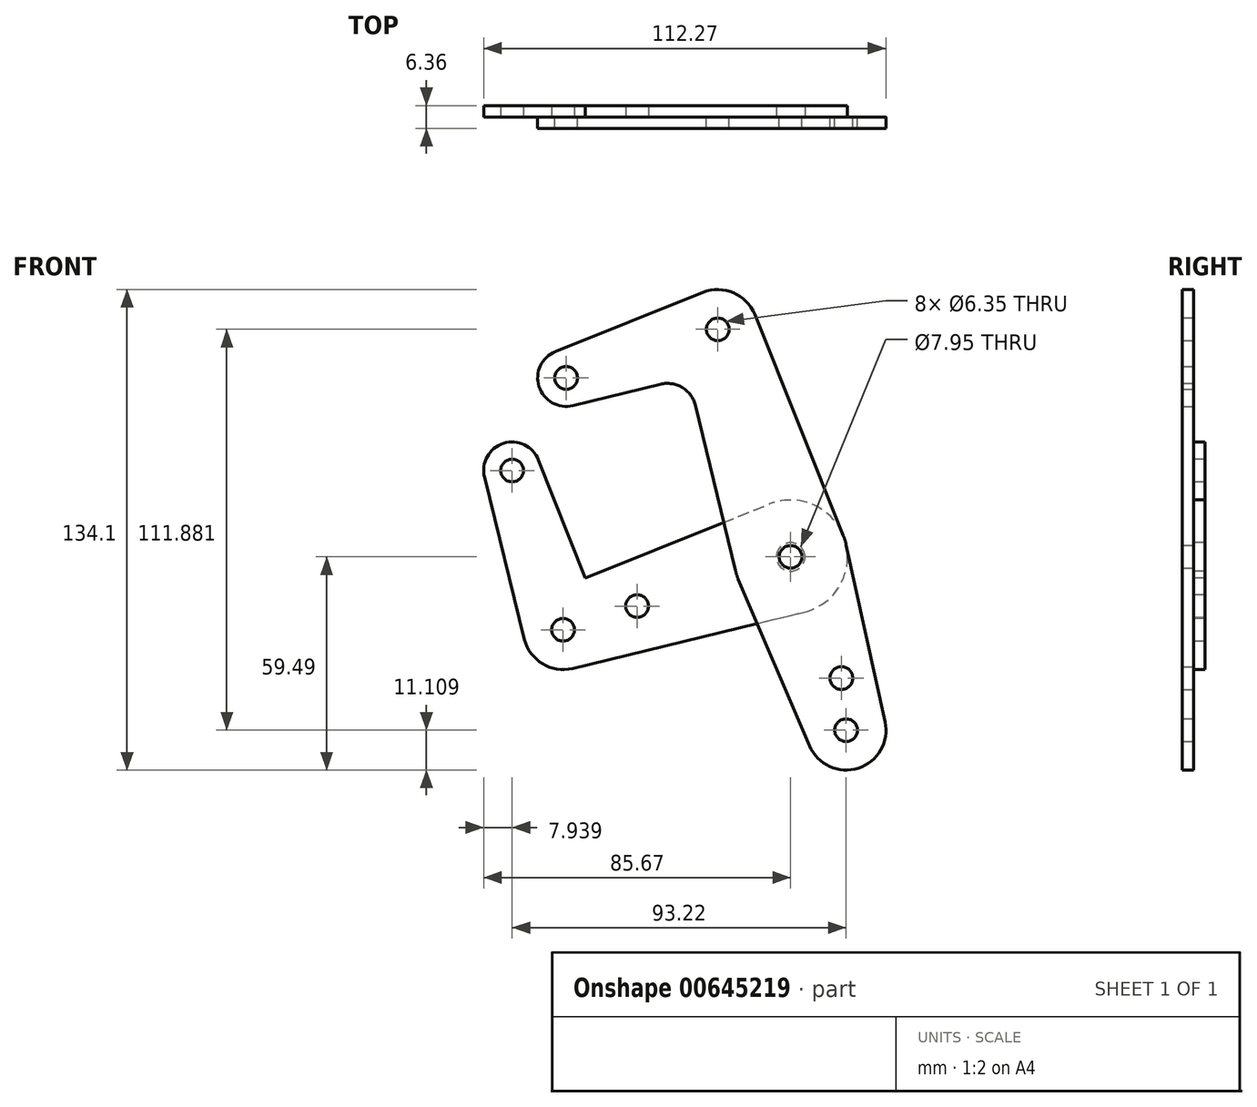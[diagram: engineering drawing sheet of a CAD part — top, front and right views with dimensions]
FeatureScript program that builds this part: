
annotation { "Feature Type Name" : "Feature", "Feature Type Description" : "" }
export const myFeature = defineFeature(function(context is Context, id is Id, definition is map)
    precondition{}
    {
        {
            var Q0;
            Q0=qCreatedBy(makeId("Front.planeOp"),FACE);
            var sketch = newSketch(context, id + "F0", { "sketchPlane" : qUnion([Q0])});
            skCircle(sketch, "E0", {"center": v(-62.66, 49.95) * mm, "radius": 7.94 * mm});
            skCircle(sketch, "E1", {"center": v(-20.33, 63.5) * mm, "radius": 11.11 * mm});
            skCircle(sketch, "E2", {"center": v(0, 0) * mm, "radius": 15.88 * mm});
            skCircle(sketch, "E3", {"center": v(15.49, -48.38) * mm, "radius": 11.11 * mm});
            skCircle(sketch, "E4", {"center": v(14.16, -33.82) * mm, "radius": 3.17 * mm});
            skLineSegment(sketch, "E5", {"start": v(-27.48, 85.85) * mm, "end": v(19.13, -59.77) * mm, "construction": true});
            skLineSegment(sketch, "E6", {"start": v(0, 0) * mm, "end": v(60.36, 19.32) * mm, "construction": true});
            skLineSegment(sketch, "E7", {"start": v(-77.14, 45.31) * mm, "end": v(-2.1, 69.33) * mm, "construction": true});
            skCircle(sketch, "E8", {"center": v(15.49, -48.38) * mm, "radius": 3.18 * mm});
            skCircle(sketch, "E9", {"center": v(0, 0) * mm, "radius": 3.98 * mm});
            skCircle(sketch, "E10", {"center": v(0, 0) * mm, "radius": 3.18 * mm});
            skCircle(sketch, "E11", {"center": v(-20.33, 63.5) * mm, "radius": 3.18 * mm});
            skCircle(sketch, "E12", {"center": v(-62.66, 49.95) * mm, "radius": 3.18 * mm});
            skLineSegment(sketch, "E13", {"start": v(14.16, -33.82) * mm, "end": v(22.72, -60.54) * mm, "construction": true});
            skLineSegment(sketch, "E14", {"start": v(-65.62, 57.31) * mm, "end": v(-24.47, 73.81) * mm});
            skLineSegment(sketch, "E15", {"start": v(-10.02, 67.64) * mm, "end": v(14.73, 5.9) * mm});
            skLineSegment(sketch, "E16", {"start": v(5.27, -52.75) * mm, "end": v(-14.6, -6.24) * mm});
            skLineSegment(sketch, "E17", {"start": v(-15.43, -3.75) * mm, "end": v(-26.63, 42.35) * mm});
            skLineSegment(sketch, "E18", {"start": v(26.34, -46) * mm, "end": v(15.5, 3.4) * mm});
            skLineSegment(sketch, "E19", {"start": v(-60.79, 42.23) * mm, "end": v(-36.23, 48.2) * mm});
            skArc(sketch, "E20.filletArc", {"start": v(-26.63, 42.35) * mm, "mid": v(-30.22, 47.27) * mm, "end": v(-36.23, 48.2) * mm});
            skLineSegment(sketch, "E21", {"start": v(0, 0) * mm, "end": v(-85.7, -27.44) * mm, "construction": true});
            skLineSegment(sketch, "E22", {"start": v(-76.14, 19.16) * mm, "end": v(-54.17, -49.48) * mm, "construction": true});
            skCircle(sketch, "E23", {"center": v(-42.85, -13.72) * mm, "radius": 3.18 * mm});
            skCircle(sketch, "E24", {"center": v(-63.5, -20.33) * mm, "radius": 11.11 * mm});
            skCircle(sketch, "E25", {"center": v(-77.73, 24.12) * mm, "radius": 7.94 * mm});
            skCircle(sketch, "E26", {"center": v(-63.5, -20.33) * mm, "radius": 3.18 * mm});
            skCircle(sketch, "E27", {"center": v(-77.73, 24.12) * mm, "radius": 3.18 * mm});
            skLineSegment(sketch, "E28", {"start": v(-70.35, 27.05) * mm, "end": v(-53.17, -16.23) * mm});
            skLineSegment(sketch, "E29", {"start": v(-85.44, 22.22) * mm, "end": v(-74.29, -23) * mm});
            skLineSegment(sketch, "E30", {"start": v(-60.88, -31.13) * mm, "end": v(3.75, -15.43) * mm});
            skLineSegment(sketch, "E31", {"start": v(-67.64, -10.02) * mm, "end": v(-5.9, 14.73) * mm});
            skSolve(sketch);
        }
        {
            var Q0;
            {var subQ4=sQuery(id+"F0.wireOp",EDGE,"E14");Q0=makeQuery(id+"F0.imprint","IMPRINT",FACE,{"disambiguationData":[TD([[makeQuery(id+"F0.imprint","IMPRINT",EDGE,{"derivedFrom":subQ4}),-1.0]])]});}
            var Q1;
            Q1=makeQuery(id+"F0.imprint","IMPRINT",FACE,{"disambiguationData":[TD([[makeQuery(id+"F0.imprint","IMPRINT",EDGE,{"derivedFrom":sQuery(id+"F0.wireOp",EDGE,"E4")}),-1.0]])]});
            var Q2;
            Q2=makeQuery(id+"F0.imprint","IMPRINT",FACE,{"disambiguationData":[TD([[makeQuery(id+"F0.imprint","IMPRINT",EDGE,{"derivedFrom":sQuery(id+"F0.wireOp",EDGE,"E9")}),-1.0]])]});
            var Q3;
            Q3=makeQuery(id+"F0.imprint","IMPRINT",FACE,{"disambiguationData":[TD([[makeQuery(id+"F0.imprint","IMPRINT",EDGE,{"derivedFrom":sQuery(id+"F0.wireOp",EDGE,"E9")}),1.0]])]});
            var Q4;
            Q4=makeQuery(id+"F0.imprint","IMPRINT",FACE,{"disambiguationData":[TD([[makeQuery(id+"F0.imprint","IMPRINT",EDGE,{"derivedFrom":sQuery(id+"F0.wireOp",EDGE,"E8")}),-1.0]])]});
            var Q5;
            Q5=makeQuery(id+"F0.imprint","IMPRINT",FACE,{"disambiguationData":[TD([[makeQuery(id+"F0.imprint","IMPRINT",EDGE,{"derivedFrom":sQuery(id+"F0.wireOp",EDGE,"E11")}),-1.0]])]});
            var Q6;
            Q6=makeQuery(id+"F0.imprint","IMPRINT",FACE,{"disambiguationData":[TD([[makeQuery(id+"F0.imprint","IMPRINT",EDGE,{"derivedFrom":sQuery(id+"F0.wireOp",EDGE,"E12")}),-1.0]])]});
            var Q7;
            {var subQ0=sQuery(id+"F0.wireOp",EDGE,"E17");var subQ1=sQuery(id+"F0.wireOp",EDGE,"E2");var subQ2=makeQuery(id+"F0.imprint","INTERSECT",VERTEX,{"derivedFrom":[subQ1,subQ0]});Q7=makeQuery(id+"F0.imprint","IMPRINT",FACE,{"disambiguationData":[TD([[makeQuery(id+"F0.imprint","IMPRINT",EDGE,{"disambiguationData":[TD([[subQ2,1.0]])],"derivedFrom":subQ1}),-1.0]])]});}
            var Q8;
            {var subQ0=sQuery(id+"F0.wireOp",EDGE,"E16");var subQ1=sQuery(id+"F0.wireOp",EDGE,"E2");var subQ2=makeQuery(id+"F0.imprint","INTERSECT",VERTEX,{"derivedFrom":[subQ1,subQ0]});Q8=makeQuery(id+"F0.imprint","IMPRINT",FACE,{"disambiguationData":[TD([[makeQuery(id+"F0.imprint","IMPRINT",EDGE,{"disambiguationData":[TD([[subQ2,-1.0]])],"derivedFrom":subQ1}),-1.0]])]});}
            extrude(context, id + "F1", {"entities" : qUnion([Q0, Q1, Q2, Q3, Q4, Q5, Q6, Q7, Q8]), "depth" : 3.17 * mm, "offsetDistance" : 25.4 * mm});
        }
        {
            var Q0;
            Q0=makeQuery(id+"F0.imprint","IMPRINT",FACE,{"disambiguationData":[TD([[makeQuery(id+"F0.imprint","IMPRINT",EDGE,{"derivedFrom":sQuery(id+"F0.wireOp",EDGE,"E23")}),-1.0]])]});
            var Q1;
            {var subQ5=sQuery(id+"F0.wireOp",EDGE,"E29");Q1=makeQuery(id+"F0.imprint","IMPRINT",FACE,{"disambiguationData":[TD([[makeQuery(id+"F0.imprint","IMPRINT",EDGE,{"derivedFrom":subQ5}),1.0]])]});}
            var Q2;
            Q2=makeQuery(id+"F0.imprint","IMPRINT",FACE,{"disambiguationData":[TD([[makeQuery(id+"F0.imprint","IMPRINT",EDGE,{"derivedFrom":sQuery(id+"F0.wireOp",EDGE,"E26")}),-1.0]])]});
            var Q3;
            {var subQ0=sQuery(id+"F0.wireOp",EDGE,"E28");var subQ1=sQuery(id+"F0.wireOp",EDGE,"E24");var subQ2=makeQuery(id+"F0.imprint","INTERSECT",VERTEX,{"derivedFrom":[subQ1,subQ0]});Q3=makeQuery(id+"F0.imprint","IMPRINT",FACE,{"disambiguationData":[TD([[makeQuery(id+"F0.imprint","IMPRINT",EDGE,{"disambiguationData":[TD([[subQ2,-1.0]])],"derivedFrom":subQ1}),-1.0]])]});}
            var Q4;
            Q4=makeQuery(id+"F0.imprint","IMPRINT",FACE,{"disambiguationData":[TD([[makeQuery(id+"F0.imprint","IMPRINT",EDGE,{"derivedFrom":sQuery(id+"F0.wireOp",EDGE,"E27")}),-1.0]])]});
            var Q5;
            Q5=makeQuery(id+"F0.imprint","IMPRINT",FACE,{"disambiguationData":[TD([[makeQuery(id+"F0.imprint","IMPRINT",EDGE,{"derivedFrom":sQuery(id+"F0.wireOp",EDGE,"E9")}),-1.0]])]});
            var Q6;
            {var subQ0=sQuery(id+"F0.wireOp",EDGE,"E16");var subQ1=sQuery(id+"F0.wireOp",EDGE,"E2");var subQ2=makeQuery(id+"F0.imprint","INTERSECT",VERTEX,{"derivedFrom":[subQ1,subQ0]});Q6=makeQuery(id+"F0.imprint","IMPRINT",FACE,{"disambiguationData":[TD([[makeQuery(id+"F0.imprint","IMPRINT",EDGE,{"disambiguationData":[TD([[subQ2,-1.0]])],"derivedFrom":subQ1}),-1.0]])]});}
            var Q7;
            {var subQ0=sQuery(id+"F0.wireOp",EDGE,"E17");var subQ1=sQuery(id+"F0.wireOp",EDGE,"E2");var subQ2=makeQuery(id+"F0.imprint","INTERSECT",VERTEX,{"derivedFrom":[subQ1,subQ0]});Q7=makeQuery(id+"F0.imprint","IMPRINT",FACE,{"disambiguationData":[TD([[makeQuery(id+"F0.imprint","IMPRINT",EDGE,{"disambiguationData":[TD([[subQ2,1.0]])],"derivedFrom":subQ1}),-1.0]])]});}
            extrude(context, id + "F2", {"entities" : qUnion([Q0, Q1, Q2, Q3, Q4, Q5, Q6, Q7]), "oppositeDirection" : true, "depth" : 3.17 * mm, "offsetDistance" : 25.4 * mm});
        }
    });
